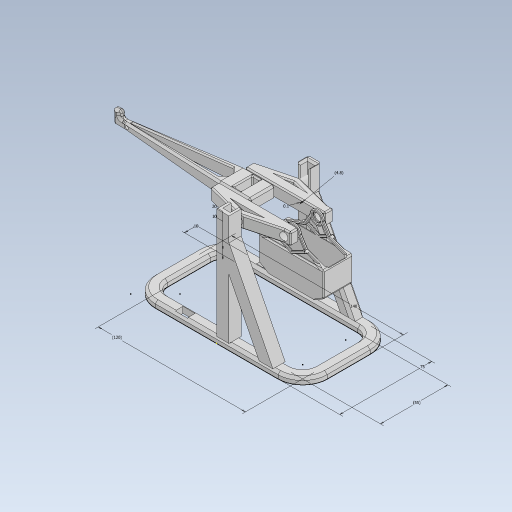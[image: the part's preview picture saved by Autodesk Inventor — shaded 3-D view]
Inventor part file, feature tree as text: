
AUTODESK INVENTOR PART (.ipt)
format: ipt  version: 2023 (Build 270158030, 158C)  size: 1,234,944 bytes
history: native  units: mm
features: sketch x25, extrude x22, chamfer x21, other x6, projected_geometry x6, mirror x5, plane x2, fillet x2
ambient origin geometry x8: Origin, YZ Plane, XZ Plane, XY Plane, X Axis, Y Axis, Z Axis, Center Point
bodies: Solid1 (feature_tree)
feature tree (89):
  sketch  "Sketch1"  dims[d0=75.0mm d1=140.0mm]
  extrude  "Extrusion1"  Depth=140.0mm
  extrude  "Extrusion2"  Depth=10.0mm
  sketch  "Sketch3"  dims[d4=20.0mm d5=5.0mm d6=0.0mm]
  extrude  "Extrusion5"  Depth=5.0mm TaperAngle=0.0deg
  extrude  "Extrusion6"  Depth=1.5mm
  extrude  "Extrusion3"  Depth=10.0mm
  extrude  "Extrusion7"  Depth=1.5mm
  extrude  "Extrusion9"  Depth=10.0mm
  extrude  "Extrusion10"  TaperAngle=0.0deg  [1 undecoded]
  extrude  "Extrusion11"  Depth=120.0mm
  plane  "Work Plane1"
  mirror  "Mirror1"
  other  "Work Point1"
  plane  "Work Plane2"
  extrude  "Extrusion12"  Depth=0.1mm
  extrude  "Extrusion13"  Depth=47.0mm
  extrude  "Extrusion14"  Depth=10.0mm
  extrude  "Extrusion15"  Depth=35.9mm
  extrude  "Extrusion17"  Depth=5.0mm
  extrude  "Extrusion18"  Depth=10.0mm
  chamfer  "Chamfer1"  Distance=90.0mm
  chamfer  "Chamfer2"  Distance=10.0mm
  chamfer  "Chamfer3"  Distance=11.0mm
  chamfer  "Chamfer4"  Distance=11.205444mm
  extrude  "Extrusion19"  TaperAngle=0.0deg  [1 undecoded]
  chamfer  "Chamfer5"  Distance=6.2mm
  chamfer  "Chamfer6"  Distance=1.9mm
  fillet  "Fillet1"  Radius=1.9mm
  chamfer  "Chamfer7"  Distance=12.0mm
  chamfer  "Chamfer8"  Distance=6.2mm
  chamfer  "Chamfer9"  Distance=7.0mm
  fillet  "Fillet2"  Radius=6.0mm
  chamfer  "Chamfer10"  Distance=3.2mm
  chamfer  "Chamfer11"  Distance=10.0mm
  chamfer  "Chamfer12"  Distance=7.0mm
  mirror  "Mirror2"
  extrude  "Extrusion20"  Depth=3.0mm
  mirror  "Mirror3"
  extrude  "Extrusion21"  Depth=35.0mm
  extrude  "Extrusion22"  Depth=7.0mm
  mirror  "Mirror4"
  chamfer  "Chamfer13"  Distance=7.0mm
  extrude  "Extrusion23"  Depth=7.0mm
  mirror  "Mirror5"
  sketch  "Sketch28"  dims[d50=10.0mm d51=90.0mm d52=0.0mm d53=10.0mm d54=0.0mm]
  chamfer  "Chamfer14"  Distance=21.0mm
  chamfer  "Chamfer15"  Distance=2.0mm
  chamfer  "Chamfer16"  Distance=6.0mm
  chamfer  "Chamfer17"  Distance=5.0mm
  chamfer  "Chamfer18"  Distance=5.0mm
  extrude  "Extrusion24"  TaperAngle=0.0deg  [1 undecoded]
  extrude  "Extrusion25"  Depth=3.0mm
  chamfer  "Chamfer19"  Distance=5.0mm
  chamfer  "Chamfer20"  Distance=21.0mm
  chamfer  "Chamfer21"  [1 undecoded]
  sketch  "Sketch6"  dims[d9=2.5mm d10=10.0mm]
  sketch  "Sketch2"  dims[d2=10.0mm d3=10.0mm]
  sketch  "Sketch4"  dims[d7=6.0mm d8=1.5mm]
  projected_geometry  "Projected Loop1"
  other  "A-frame"
  sketch  "Sketch7"  dims[d11=5.0mm d12=1.5mm]
  projected_geometry  "Projected Loop2"
  other  "upright"
  sketch  "Sketch9"  dims[d13=6.0mm d14=10.0mm]
  projected_geometry  "Projected Loop3"
  sketch  "Sketch10"  dims[d15=60.0mm d16=0.0mm d17=0.0mm]
  sketch  "Sketch12"  dims[d18=55.0mm d19=120.0mm]
  sketch  "Sketch13"  dims[d22=0.1mm d23=0.1mm]
  sketch  "Sketch14"  dims[d24=5.0mm d25=0.0mm d30=47.0mm]
  other  "pivot"
  sketch  "Sketch15"  dims[d31=15.0mm d32=10.0mm]
  sketch  "Sketch16"  dims[d33=54.5mm d34=35.9mm]
  sketch  "Sketch17"  dims[d35=55.9mm d36=5.0mm]
  other  "throw-arm-top"
  sketch  "Sketch18"  dims[d37=5.0mm d38=10.0mm]
  sketch  "Sketch20"  dims[d39=25.0mm]
  sketch  "Sketch21"  dims[d40=25.0mm]
  sketch  "Sketch22"  dims[d41=0.1mm]
  sketch  "Sketch24"  dims[d42=5.0mm d43=5.0mm d44=0.0mm d45=0.0mm]
  other  "counterweight"
  sketch  "Sketch25"  dims[d47=10.0mm]
  projected_geometry  "Projected Loop5"
  sketch  "Sketch26"  dims[d48=0.9mm]
  projected_geometry  "Projected Loop6"
  sketch  "Sketch27"  dims[d49=0.5mm]
  projected_geometry  "Projected Loop7"
  sketch  "Sketch29"  dims[d60=5.0mm]
  sketch  "Sketch30"  dims[d61=5.0mm d62=11.0mm d63=11.205444mm d64=0.0mm d65=0.0mm d66=6.2mm d67=1.9mm d68=1.9mm d69=12.0mm d70=6.2mm d71=7.0mm d72=0.0mm d73=6.0mm d74=3.2mm d75=10.0mm d76=0.0mm d77=7.0mm d78=30.0mm d79=35.0mm d80=7.0mm d82=7.0mm d83=7.0mm d84=21.0mm d85=2.0mm d86=8.0mm d87=0.0mm d88=0.0mm d89=6.0mm d90=5.0mm d91=5.0mm d92=0.0mm d93=0.0mm d94=5.0mm d95=5.0mm d96=21.0mm d98=0.0mm d99=5.0mm d100=10.0mm d101=8.0mm d102=8.0mm d103=120.0mm d104=10.0mm d105=5.0mm d106=0.0mm d107=0.0mm d108=5.0mm d109=12.0mm d110=0.0mm d111=0.0mm d119=6.0mm d120=5.0mm d121=10.0mm d122=0.0mm d123=7.0mm d124=6.0mm d125=0.0mm d126=1.0mm d127=2.0mm d128=45.0deg d129=1.0mm d130=2.0mm d131=45.0deg d132=1.0mm d133=2.0mm d134=45.0deg d135=1.0mm d136=2.0mm d137=45.0deg d138=2.5mm d139=2.8mm d140=12.0mm d141=0.0mm d142=0.0mm d143=25.0mm d144=6.0mm d145=2.0mm d146=2.0mm d147=45.0deg d148=2.0mm d149=2.0mm d150=45.0deg d151=2.0mm d152=2.0mm d153=2.0mm d154=45.0deg d155=1.0mm d156=2.0mm d157=45.0deg d158=1.5mm d159=2.0mm d160=45.0deg d161=2.0mm d162=1.5mm d163=2.0mm d164=45.0deg d165=2.0mm d166=2.0mm d167=45.0deg d168=1.5mm d169=2.0mm d170=45.0deg d171=0.5mm d172=2.0mm d173=8.0mm d174=5.0mm d175=16.0mm d176=6.0mm d177=20.0mm d178=5.0mm d179=16.0mm d180=8.0mm d181=8.0mm d182=2.0mm d183=2.0mm d184=0.0mm d185=2.0mm d186=0.0mm d187=1.5mm d188=0.0mm d189=1.5mm d190=2.0mm d191=45.0deg d192=1.0mm d193=1.0mm d194=1.0mm d195=1.0mm d196=1.5mm d197=0.0mm d198=0.1mm d199=4.8mm d200=1.0mm d201=2.0mm d202=45.0deg d203=0.5mm d204=2.0mm d205=45.0deg d206=0.5mm d207=2.0mm d208=45.0deg d209=0.5mm d210=2.0mm d211=45.0deg d212=0.5mm d213=2.0mm d214=45.0deg d215=2.0mm d216=1.0mm d217=3.0mm d218=3.0mm d219=2.5mm d220=2.5mm d221=0.0mm d222=0.0mm d223=1.0mm d224=1.0mm d225=3.0mm d226=3.0mm d227=0.0mm d228=0.0mm d229=2.0mm d230=2.0mm d231=45.0deg d232=4.0mm d233=2.0mm d234=45.0deg d235=1.0mm d236=2.0mm d237=45.0deg]
note: 4 required parameter values undecoded (feature->parameter linkage not recoverable at this tier; creation-order binding heuristic only, values carry confidence <= 0.55)
